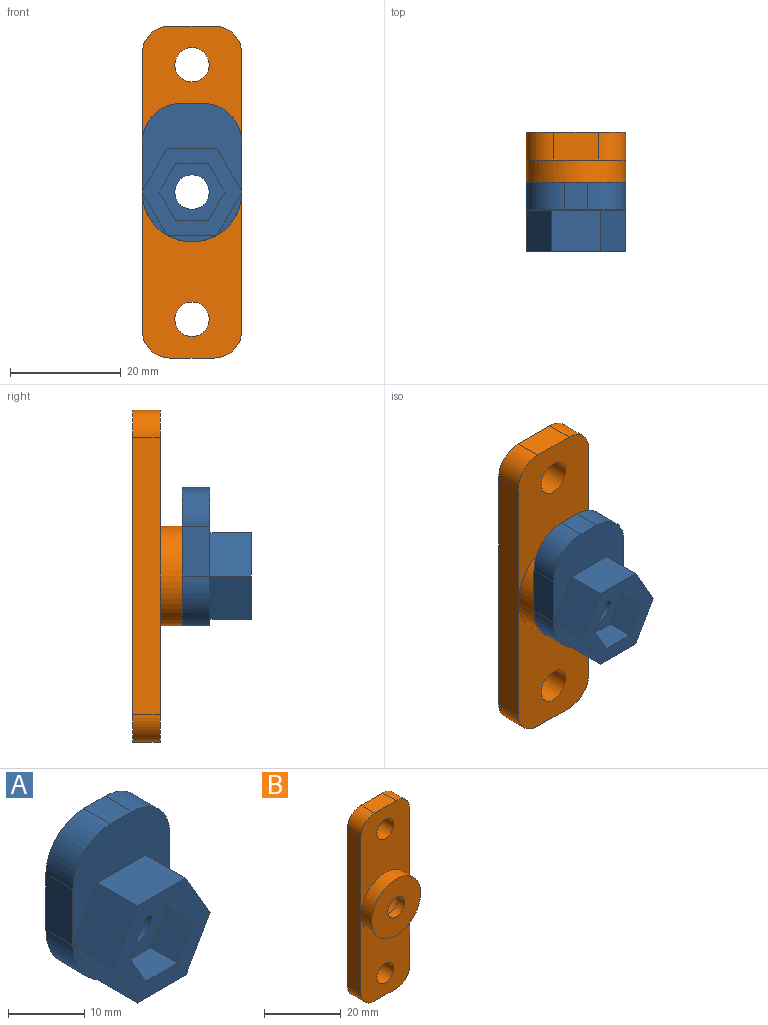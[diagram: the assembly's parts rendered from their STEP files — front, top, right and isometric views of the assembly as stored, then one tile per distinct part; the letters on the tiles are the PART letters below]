
ASSEMBLY  parts=2 mates=1
PART A: 26 faces, bbox 18x12.5x25 mm
  f0: plane 11.78x10.2mm, normal (0,-1,0), area 59.9mm2, adj f7,f19,f20,f21,f22,f23,f24
  f1: plane 9x1.21mm, normal (0,-1,0), area 7.3mm2, adj f5,f13
  f2: plane 7.79x4.5mm, normal (0,-1,0), area 7.3mm2, adj f5,f18
  f3: plane 18x16mm, normal (0,-1,0), area 161.7mm2, adj f4,f6,f8,f11,f12,f15,f16,f17
  f4: plane 9x5mm, normal (-1,0,0), area 45mm2, adj f3,f5,f10,f12
  f5: cylinder r=9mm len=18mm, axis (0,1,0), area 141.4mm2, adj f1,f2,f4,f6,f9,f10
  f6: plane 9x5mm, normal (1,0,0), area 45mm2, adj f3,f5,f10,f11
  f7: cylinder r=3.1mm len=7.5mm, axis (0,1,0), area 146.1mm2, adj f0,f10
  f8: plane 5x4mm, normal (0,0,1), area 20mm2, adj f3,f10,f11,f12
  f9: plane 7.79x4.5mm, normal (0,-1,0), area 7.3mm2, adj f5,f14
  f10: plane 25x18mm, normal (0,1,0), area 364mm2, adj f4,f5,f6,f7,f8,f11,f12
  f11: cylinder r=7mm len=7mm, axis (0,1,0), area 55mm2, adj f3,f6,f8,f10
  f12: cylinder r=7mm len=7mm, axis (0,1,0), area 55mm2, adj f3,f4,f8,f10
  f13: plane 9x7.5mm, normal (0,0,-1), area 67.5mm2, adj f1,f14,f18,f25
  f14: plane 7.79x7.5mm, normal (0.87,0,-0.5), area 67.5mm2, adj f9,f13,f15,f25
  f15: plane 7.79x7.5mm, normal (0.87,0,0.5), area 67.5mm2, adj f3,f14,f16,f25
  f16: plane 9x7.5mm, normal (0,0,1), area 67.5mm2, adj f3,f15,f17,f25
  f17: plane 7.79x7.5mm, normal (-0.87,0,0.5), area 67.5mm2, adj f3,f16,f18,f25
  f18: plane 7.79x7.5mm, normal (-0.87,0,-0.5), area 67.5mm2, adj f2,f13,f17,f25
  f19: plane 5.89x5mm, normal (0,0,-1), area 29.4mm2, adj f0,f20,f24,f25
  f20: plane 5.1x5mm, normal (-0.87,0,-0.5), area 29.4mm2, adj f0,f19,f21,f25
  f21: plane 5.1x5mm, normal (-0.87,0,0.5), area 29.4mm2, adj f0,f20,f22,f25
  f22: plane 5.89x5mm, normal (0,0,1), area 29.4mm2, adj f0,f21,f23,f25
  f23: plane 5.1x5mm, normal (0.87,0,0.5), area 29.4mm2, adj f0,f22,f24,f25
  f24: plane 5.1x5mm, normal (0.87,0,-0.5), area 29.4mm2, adj f0,f19,f23,f25
  f25: plane 18x15.59mm, normal (0,-1,0), area 120.3mm2, adj f13,f14,f15,f16,f17,f18,f19,f20
PART B: 18 faces, bbox 18x9x60 mm
  f0: plane 30x18mm, normal (0,-1,0), area 371.8mm2, adj f1,f2,f4,f6,f10,f13,f14
  f1: plane 8x5mm, normal (0,0,1), area 40mm2, adj f0,f9,f10,f13
  f2: plane 50x5mm, normal (-1,0,0), area 250mm2, adj f0,f8,f9,f10,f11
  f3: plane 8x5mm, normal (0,0,-1), area 40mm2, adj f8,f9,f11,f12
  f4: cylinder r=3.1mm len=6.2mm, axis (0,1,0), area 97.4mm2, adj f0,f9
  f5: cylinder r=3.1mm len=6.2mm, axis (0,1,0), area 97.4mm2, adj f8,f9
  f6: plane 50x5mm, normal (1,0,0), area 250mm2, adj f0,f8,f9,f12,f13
  f7: cylinder r=3.1mm len=6.2mm, axis (0,1,0), area 48.7mm2, adj f15,f17
  f8: plane 30x18mm, normal (0,-1,0), area 371.8mm2, adj f2,f3,f5,f6,f11,f12,f14
  f9: plane 60x18mm, normal (0,1,0), area 916.4mm2, adj f1,f2,f3,f4,f5,f6,f10,f11
  f10: cylinder r=5mm len=5mm, axis (0,-1,0), area 39.3mm2, adj f0,f1,f2,f9
  f11: cylinder r=5mm len=5mm, axis (0,1,0), area 39.3mm2, adj f2,f3,f8,f9
  f12: cylinder r=5mm len=5mm, axis (0,-1,0), area 39.3mm2, adj f3,f6,f8,f9
  f13: cylinder r=5mm len=5mm, axis (0,1,0), area 39.3mm2, adj f0,f1,f6,f9
  f14: cylinder r=9mm len=18mm, axis (0,1,0), area 226.2mm2, adj f0,f8,f15
  f15: plane 18x18mm, normal (0,-1,0), area 224.3mm2, adj f7,f14
  f16: cylinder r=5.1mm len=10.2mm, axis (0,1,0), area 208.3mm2, adj f9,f17
  f17: plane 10.2x10.2mm, normal (0,1,0), area 51.5mm2, adj f7,f16
PLACE A t=(14.59,23.61,3.79)mm
PLACE B t=(14.59,32.61,3.79)mm fixed
MATE revolute B.f14 <-> A.f5  axis (0,-1,0) through (14.59,23.61,3.79)mm
